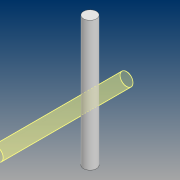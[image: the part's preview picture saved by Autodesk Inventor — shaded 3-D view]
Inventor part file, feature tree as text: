
AUTODESK INVENTOR PART (.ipt)
format: ipt  version: 2021 (Build 250183000, 183)  size: 80,896 bytes
history: native  units: mm
features: extrude x1, sketch x1
ambient origin geometry x8: Origin, YZ Plane, XZ Plane, XY Plane, X Axis, Y Axis, Z Axis, Center Point
bodies: Solid1 (feature_tree)
feature tree (2):
  extrude  "Extrusion1"  Depth=120.0mm TaperAngle=0.0deg
  sketch  "Sketch1"  dims[d0=10.0mm d1=120.0mm d2=0.0mm]
